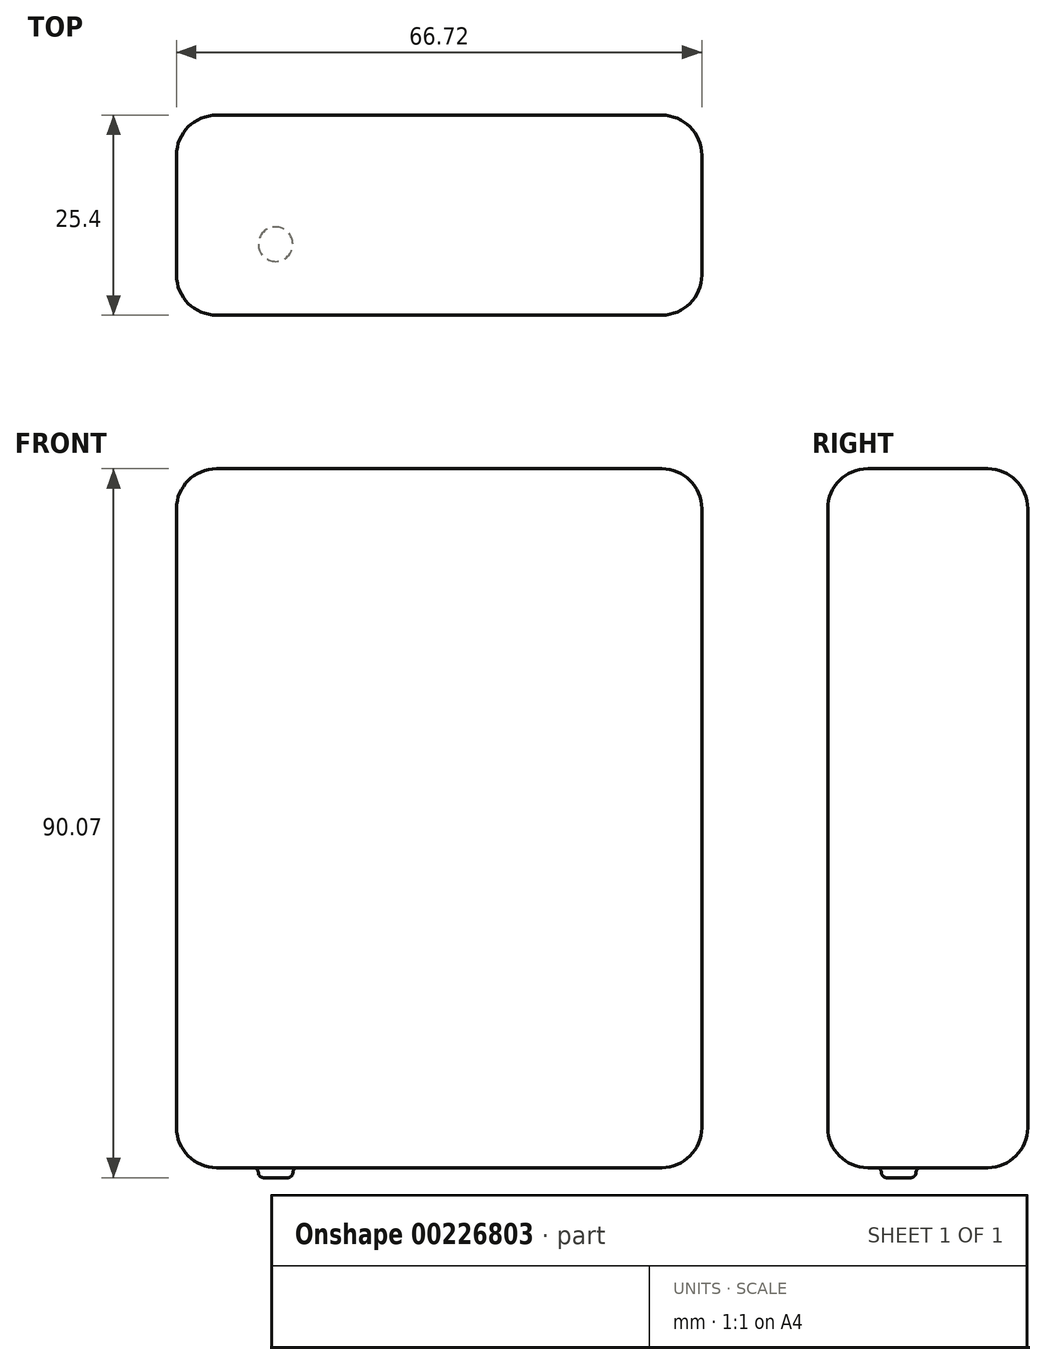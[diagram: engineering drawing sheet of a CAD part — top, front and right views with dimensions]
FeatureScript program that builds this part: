
annotation { "Feature Type Name" : "Feature", "Feature Type Description" : "" }
export const myFeature = defineFeature(function(context is Context, id is Id, definition is map)
    precondition{}
    {
        {
            var Q0;
            Q0=qCreatedBy(makeId("Front.planeOp"),FACE);
            var sketch = newSketch(context, id + "F0", { "sketchPlane" : qUnion([Q0])});
            skLineSegment(sketch, "E0.bottom", {"start": v(-33.24, 40.84) * mm, "end": v(33.48, 40.84) * mm});
            skLineSegment(sketch, "E0.top", {"start": v(-33.24, -47.96) * mm, "end": v(33.48, -47.96) * mm});
            skLineSegment(sketch, "E0.left", {"start": v(-33.24, 40.84) * mm, "end": v(-33.24, -47.96) * mm});
            skLineSegment(sketch, "E0.right", {"start": v(33.48, 40.84) * mm, "end": v(33.48, -47.96) * mm});
            skSolve(sketch);
        }
        {
            var Q0;
            Q0 = qSketchRegion(id + "F0", true);
            extrude(context, id + "F1", {"entities" : qUnion([Q0]), "depth" : 25.4 * mm});
        }
        {
            var Q0;
            Q0=makeQuery(id+"F1.opExtrude","CAP_EDGE",EDGE,{"disambiguationData":[OSD([sQuery(id+"F0.wireOp",EDGE,"E0.right")])],"isStart":false});
            var Q1;
            Q1=makeQuery(id+"F1.opExtrude","CAP_EDGE",EDGE,{"disambiguationData":[OSD([sQuery(id+"F0.wireOp",EDGE,"E0.top")])],"isStart":false});
            var Q2;
            Q2=makeQuery(id+"F1.opExtrude","SWEPT_FACE",FACE,{"disambiguationData":[OSD([sQuery(id+"F0.wireOp",EDGE,"E0.right")])]});
            var Q3;
            Q3=makeQuery(id+"F1.opExtrude","CAP_EDGE",EDGE,{"disambiguationData":[OSD([sQuery(id+"F0.wireOp",EDGE,"E0.bottom")])],"isStart":false});
            var Q4;
            Q4=makeQuery(id+"F1.opExtrude","SWEPT_FACE",FACE,{"disambiguationData":[OSD([sQuery(id+"F0.wireOp",EDGE,"E0.left")])]});
            var Q5;
            Q5=makeQuery(id+"F1.opExtrude","CAP_EDGE",EDGE,{"disambiguationData":[OSD([sQuery(id+"F0.wireOp",EDGE,"E0.bottom")])],"isStart":true});
            var Q6;
            Q6=makeQuery(id+"F1.opExtrude","SWEPT_EDGE",EDGE,{"disambiguationData":[OSD([sQuery(id+"F0.wireOp",EDGE,"E0.bottom"),sQuery(id+"F0.wireOp",EDGE,"E0.left")])]});
            var Q7;
            Q7=makeQuery(id+"F1.opExtrude","SWEPT_FACE",FACE,{"disambiguationData":[OSD([sQuery(id+"F0.wireOp",EDGE,"E0.bottom")])]});
            var Q8;
            Q8=makeQuery(id+"F1.opExtrude","SWEPT_EDGE",EDGE,{"disambiguationData":[OSD([sQuery(id+"F0.wireOp",EDGE,"E0.bottom"),sQuery(id+"F0.wireOp",EDGE,"E0.right")])]});
            var Q9;
            Q9=makeQuery(id+"F1.opExtrude","CAP_FACE",FACE,{"disambiguationData":[OSD([sQuery(id+"F0.wireOp",EDGE,"E0.bottom"),sQuery(id+"F0.wireOp",EDGE,"E0.top"),sQuery(id+"F0.wireOp",EDGE,"E0.left"),sQuery(id+"F0.wireOp",EDGE,"E0.right")])],"isStart":true});
            var Q10;
            Q10=makeQuery(id+"F1.opExtrude","CAP_FACE",FACE,{"disambiguationData":[OSD([sQuery(id+"F0.wireOp",EDGE,"E0.bottom"),sQuery(id+"F0.wireOp",EDGE,"E0.top"),sQuery(id+"F0.wireOp",EDGE,"E0.left"),sQuery(id+"F0.wireOp",EDGE,"E0.right")])],"isStart":false});
            var Q11;
            Q11=makeQuery(id+"F1.opExtrude","SWEPT_EDGE",EDGE,{"disambiguationData":[OSD([sQuery(id+"F0.wireOp",EDGE,"E0.top"),sQuery(id+"F0.wireOp",EDGE,"E0.right")])]});
            var Q12;
            Q12=makeQuery(id+"F1.opExtrude","SWEPT_FACE",FACE,{"disambiguationData":[OSD([sQuery(id+"F0.wireOp",EDGE,"E0.top")])]});
            var Q13;
            Q13=makeQuery(id+"F1.opExtrude","CAP_EDGE",EDGE,{"disambiguationData":[OSD([sQuery(id+"F0.wireOp",EDGE,"E0.right")])],"isStart":true});
            var Q14;
            Q14=makeQuery(id+"F1.opExtrude","CAP_EDGE",EDGE,{"disambiguationData":[OSD([sQuery(id+"F0.wireOp",EDGE,"E0.top")])],"isStart":true});
            var Q15;
            Q15=makeQuery(id+"F1.opExtrude","CAP_EDGE",EDGE,{"disambiguationData":[OSD([sQuery(id+"F0.wireOp",EDGE,"E0.left")])],"isStart":true});
            var Q16;
            Q16=makeQuery(id+"F1.opExtrude","CAP_EDGE",EDGE,{"disambiguationData":[OSD([sQuery(id+"F0.wireOp",EDGE,"E0.left")])],"isStart":false});
            var Q17;
            Q17=makeQuery(id+"F1.opExtrude","SWEPT_EDGE",EDGE,{"disambiguationData":[OSD([sQuery(id+"F0.wireOp",EDGE,"E0.top"),sQuery(id+"F0.wireOp",EDGE,"E0.left")])]});
            fillet(context, id + "F2", {"entities" : qUnion([Q0, Q1, Q2, Q3, Q4, Q5, Q6, Q7, Q8, Q9, Q10, Q11, Q12, Q13, Q14, Q15, Q16, Q17]), "radius" : 5.08 * mm, "tangentPropagation" : true, "allowEdgeOverflow" : false});
        }
        {
            var Q0;
            Q0=makeQuery(id+"F1.opExtrude","SWEPT_FACE",FACE,{"disambiguationData":[OSD([sQuery(id+"F0.wireOp",EDGE,"E0.top")])]});
            var sketch = newSketch(context, id + "F3", { "sketchPlane" : qUnion([Q0])});
            skCircle(sketch, "E1", {"center": v(-20.66, 16.38) * mm, "radius": 2.19 * mm});
            skSolve(sketch);
        }
        {
            var Q0;
            Q0=makeQuery(id+"F3.imprint","IMPRINT",FACE,{"disambiguationData":[TD([[makeQuery(id+"F3.imprint","IMPRINT",EDGE,{"derivedFrom":sQuery(id+"F3.wireOp",EDGE,"E1")}),1.0]])]});
            var Q1;
            Q1=sQuery(id+"F3.wireOp",EDGE,"E1");
            extrude(context, id + "F4", {"entities" : qUnion([Q0]), "operationType" : NewBodyOperationType.ADD, "surfaceEntities" : qUnion([Q1]), "depth" : 1.27 * mm});
        }
        {
            var Q0;
            Q0=makeQuery(id+"F4.opExtrude","CAP_FACE",FACE,{"disambiguationData":[OSD([sQuery(id+"F3.wireOp",EDGE,"E1")])],"isStart":false});
            var Q1;
            Q1=makeQuery(id+"F4.opExtrude","CAP_EDGE",EDGE,{"disambiguationData":[OSD([sQuery(id+"F3.wireOp",EDGE,"E1")])],"isStart":true});
            var Q2;
            Q2=makeQuery(id+"F4.opExtrude","SWEPT_FACE",FACE,{"disambiguationData":[OSD([sQuery(id+"F3.wireOp",EDGE,"E1")])]});
            fillet(context, id + "F5", {"entities" : qUnion([Q0, Q1, Q2]), "radius" : 0.64 * mm, "tangentPropagation" : true, "allowEdgeOverflow" : false});
        }
    });
